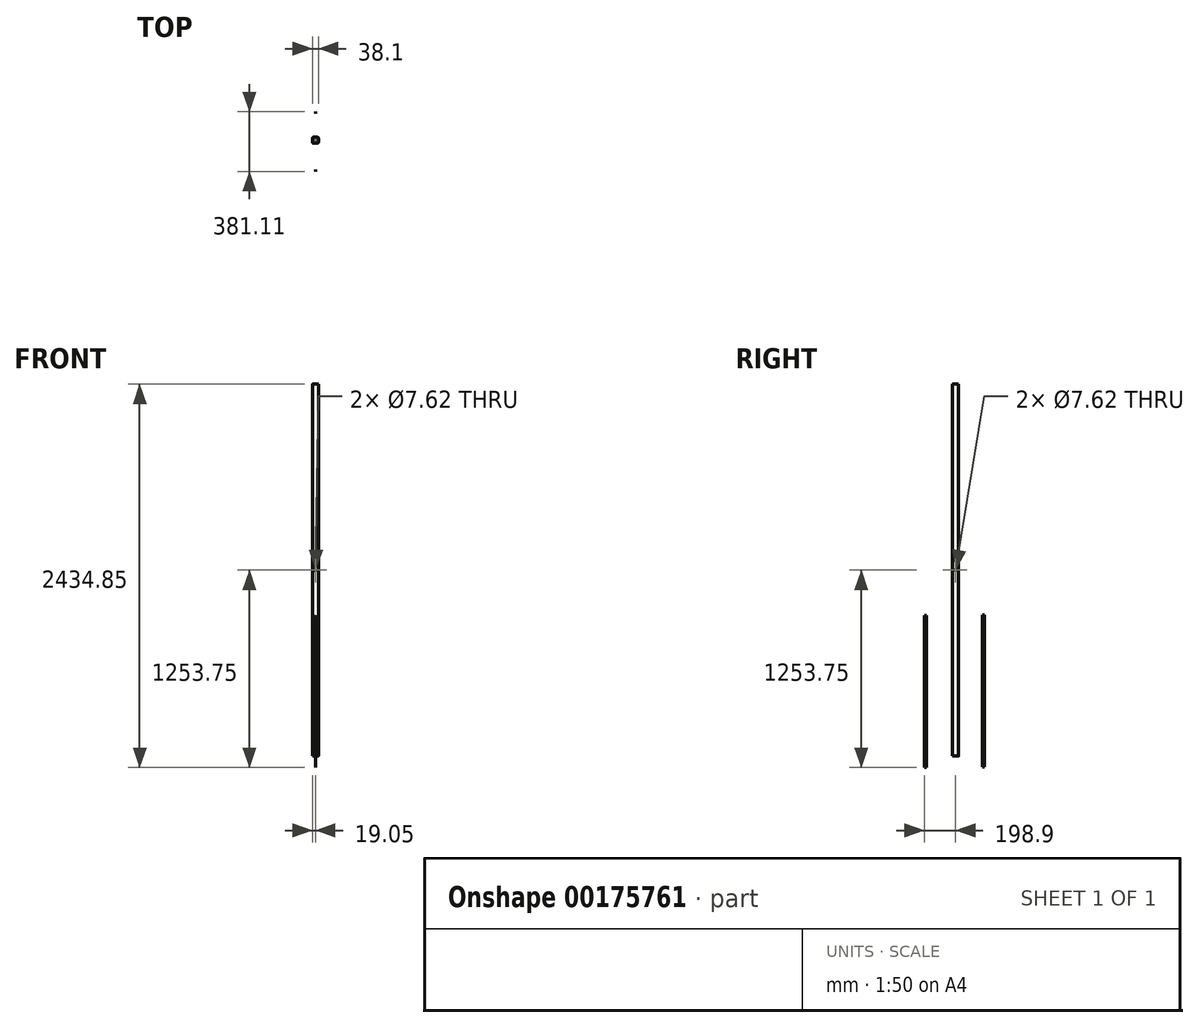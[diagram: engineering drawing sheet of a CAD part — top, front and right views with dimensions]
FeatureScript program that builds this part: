
annotation { "Feature Type Name" : "Feature", "Feature Type Description" : "" }
export const myFeature = defineFeature(function(context is Context, id is Id, definition is map)
    precondition{}
    {
        {
            var Q0;
            Q0=qCreatedBy(makeId("Top.planeOp"),FACE);
            var sketch = newSketch(context, id + "F0", { "sketchPlane" : qUnion([Q0])});
            skLineSegment(sketch, "E0.bottom", {"start": v(12.7, 19.05) * mm, "end": v(-12.7, 19.05) * mm});
            skLineSegment(sketch, "E0.top", {"start": v(12.7, -19.05) * mm, "end": v(-12.7, -19.05) * mm});
            skLineSegment(sketch, "E0.left", {"start": v(19.05, 12.7) * mm, "end": v(19.05, -12.7) * mm});
            skLineSegment(sketch, "E0.right", {"start": v(-19.05, 12.7) * mm, "end": v(-19.05, -12.7) * mm});
            skPoint(sketch, "E0.middle", {"position": v(0, 0) * mm});
            skPoint(sketch, "E1.visualSharp", {"position": v(-19.05, 19.05) * mm});
            skArc(sketch, "E1.filletArc", {"start": v(-12.7, 19.05) * mm, "mid": v(-17.2, 17.2) * mm, "end": v(-19.05, 12.7) * mm});
            skPoint(sketch, "E2.visualSharp", {"position": v(19.05, 19.05) * mm});
            skArc(sketch, "E2.filletArc", {"start": v(19.05, 12.7) * mm, "mid": v(17.2, 17.2) * mm, "end": v(12.7, 19.05) * mm});
            skPoint(sketch, "E3.visualSharp", {"position": v(19.05, -19.05) * mm});
            skArc(sketch, "E3.filletArc", {"start": v(12.7, -19.05) * mm, "mid": v(17.2, -17.2) * mm, "end": v(19.05, -12.7) * mm});
            skPoint(sketch, "E4.visualSharp", {"position": v(-19.05, -19.05) * mm});
            skArc(sketch, "E4.filletArc", {"start": v(-19.05, -12.7) * mm, "mid": v(-17.2, -17.2) * mm, "end": v(-12.7, -19.05) * mm});
            skSolve(sketch);
        }
        {
            var Q0;
            Q0=qSketchRegion(id+"F0",true);
            extrude(context, id + "F1", {"entities" : qUnion([Q0]), "depth" : 2362.2 * mm});
        }
        {
            var Q0;
            Q0=qCreatedBy(makeId("Right.planeOp"),FACE);
            var sketch = newSketch(context, id + "F2", { "sketchPlane" : qUnion([Q0])});
            skLineSegment(sketch, "E5.bottom", {"start": v(-186.2, -72.65) * mm, "end": v(-198.9, -72.65) * mm});
            skLineSegment(sketch, "E5.top", {"start": v(-186.2, 892.55) * mm, "end": v(-198.9, 892.55) * mm});
            skLineSegment(sketch, "E5.left", {"start": v(-186.2, -72.65) * mm, "end": v(-186.2, 892.55) * mm});
            skLineSegment(sketch, "E5.right", {"start": v(-198.9, -72.65) * mm, "end": v(-198.9, 892.55) * mm});
            skPoint(sketch, "E5.middle", {"position": v(-192.55, 409.95) * mm});
            skSolve(sketch);
        }
        {
            var Q0;
            Q0=qCreatedBy(makeId("Right.planeOp"),FACE);
            var sketch = newSketch(context, id + "F3", { "sketchPlane" : qUnion([Q0])});
            skLineSegment(sketch, "E6.bottom", {"start": v(182.21, -70.47) * mm, "end": v(169.51, -70.47) * mm});
            skLineSegment(sketch, "E6.top", {"start": v(182.21, 894.73) * mm, "end": v(169.51, 894.73) * mm});
            skLineSegment(sketch, "E6.left", {"start": v(182.21, -70.47) * mm, "end": v(182.21, 894.73) * mm});
            skLineSegment(sketch, "E6.right", {"start": v(169.51, -70.47) * mm, "end": v(169.51, 894.73) * mm});
            skPoint(sketch, "E6.middle", {"position": v(175.86, 412.13) * mm});
            skSolve(sketch);
        }
        {
            var Q0;
            Q0=makeQuery(id+"F2.imprint","IMPRINT",FACE,{"disambiguationData":[TD([[makeQuery(id+"F2.imprint","IMPRINT",EDGE,{"derivedFrom":sQuery(id+"F2.wireOp",EDGE,"E5.bottom")}),-1.0]])]});
            extrude(context, id + "F4", {"entities" : qUnion([Q0]), "depth" : 0.25 * mm});
        }
        {
            var Q0;
            Q0=makeQuery(id+"F3.imprint","IMPRINT",FACE,{"disambiguationData":[TD([[makeQuery(id+"F3.imprint","IMPRINT",EDGE,{"derivedFrom":sQuery(id+"F3.wireOp",EDGE,"E6.bottom")}),-1.0]])]});
            extrude(context, id + "F5", {"entities" : qUnion([Q0]), "depth" : 0.25 * mm});
        }
        {
            var Q0;
            Q0=makeQuery(id+"F1.opExtrude","SWEPT_FACE",FACE,{"disambiguationData":[OSD([sQuery(id+"F0.wireOp",EDGE,"E0.top")])]});
            var sketch = newSketch(context, id + "F6", { "sketchPlane" : qUnion([Q0])});
            skLineSegment(sketch, "E7", {"start": v(0, 0) * mm, "end": v(0, 1181.1) * mm});
            skCircle(sketch, "E8", {"center": v(0, 1181.1) * mm, "radius": 3.81 * mm});
            skSolve(sketch);
        }
        {
            var Q0;
            Q0 = qSketchRegion(id + "F6", true);
            extrude(context, id + "F7", {"entities" : qUnion([Q0]), "operationType" : NewBodyOperationType.REMOVE, "oppositeDirection" : true, "depth" : 38.1 * mm});
        }
        {
            var Q0;
            Q0=makeQuery(id+"F1.opExtrude","SWEPT_FACE",FACE,{"disambiguationData":[OSD([sQuery(id+"F0.wireOp",EDGE,"E0.left")])]});
            var sketch = newSketch(context, id + "F8", { "sketchPlane" : qUnion([Q0])});
            skLineSegment(sketch, "E9", {"start": v(0, 0) * mm, "end": v(0, 1181.1) * mm});
            skCircle(sketch, "E10", {"center": v(0, 1181.1) * mm, "radius": 3.81 * mm});
            skSolve(sketch);
        }
        {
            var Q0;
            Q0 = qSketchRegion(id + "F8", true);
            extrude(context, id + "F9", {"entities" : qUnion([Q0]), "operationType" : NewBodyOperationType.REMOVE, "oppositeDirection" : true, "depth" : 38.1 * mm});
        }
    });
